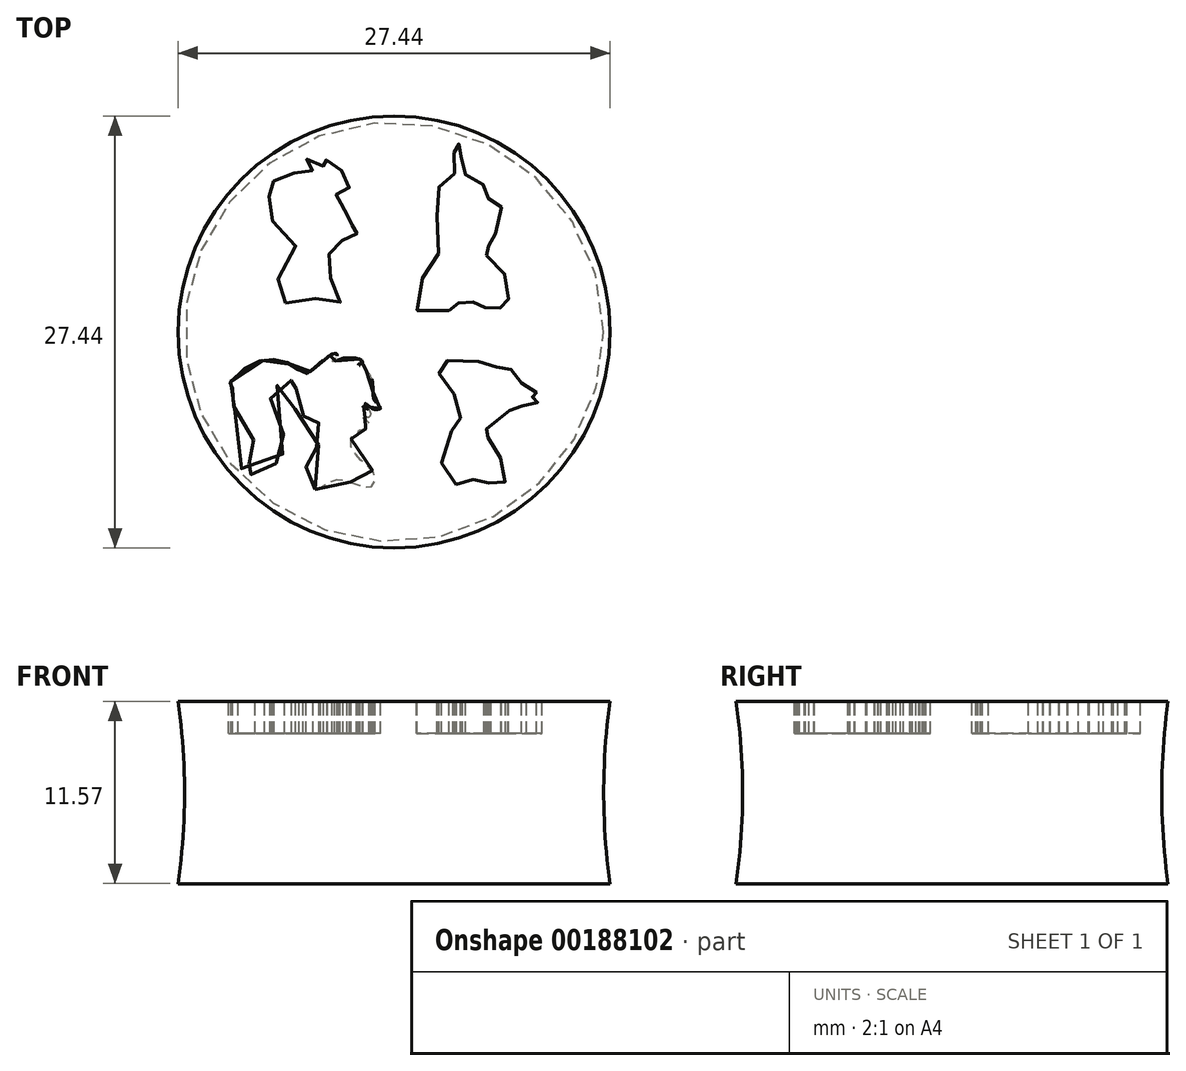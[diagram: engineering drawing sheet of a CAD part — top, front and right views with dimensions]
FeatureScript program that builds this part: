
annotation { "Feature Type Name" : "Feature", "Feature Type Description" : "" }
export const myFeature = defineFeature(function(context is Context, id is Id, definition is map)
    precondition{}
    {
        {
            var Q0;
            Q0=qCreatedBy(makeId("Front.planeOp"),FACE);
            var sketch = newSketch(context, id + "F0", { "sketchPlane" : qUnion([Q0])});
            skLineSegment(sketch, "E0", {"start": v(0, 0) * mm, "end": v(0, -11.57) * mm});
            skLineSegment(sketch, "E1", {"start": v(0, -11.57) * mm, "end": v(13.72, -11.57) * mm});
            skLineSegment(sketch, "E2", {"start": v(13.72, 0) * mm, "end": v(0, 0) * mm});
            skArc(sketch, "E3", {"start": v(13.72, 0) * mm, "mid": v(13.31, -5.79) * mm, "end": v(13.72, -11.57) * mm});
            skSolve(sketch);
        }
        {
            var Q0;
            Q0 = qSketchRegion(id + "F0", true);
            var Q1;
            Q1=sQuery(id+"F0.wireOp",EDGE,"E0");
            revolve(context, id + "F1", {"entities" : qUnion([Q0]), "axis" : qUnion([Q1]), "revolveType" : RevolveType.FULL});
        }
        {
            var Q0;
            Q0=qCreatedBy(makeId("Top.planeOp"),FACE);
            var sketch = newSketch(context, id + "F2", { "sketchPlane" : qUnion([Q0])});
            skFitSpline(sketch, "E4", {"points": [v(-6.9, 1.82) * mm, v(-6.65, 1.93) * mm, v(-6.33, 2.08) * mm, v(-6, 2.27) * mm, v(-5.69, 2.32) * mm, v(-5.44, 2.29) * mm, v(-5.23, 2.26) * mm, v(-4.96, 2.1) * mm, v(-4.72, 1.96) * mm, v(-4.48, 1.85) * mm, v(-4.2, 1.76) * mm, v(-3.95, 1.65) * mm, v(-3.71, 1.64) * mm, v(-3.5, 1.72) * mm, v(-3.43, 1.82) * mm, v(-3.43, 1.96) * mm, v(-3.46, 2.1) * mm, v(-3.5, 2.24) * mm, v(-3.53, 2.4) * mm, v(-3.6, 2.65) * mm, v(-3.67, 2.75) * mm, v(-3.82, 3.04) * mm, v(-3.94, 3.22) * mm, v(-4.01, 3.39) * mm, v(-4.1, 3.55) * mm, v(-4.2, 3.67) * mm, v(-4.2, 3.78) * mm, v(-4.22, 4.06) * mm, v(-4.24, 4.26) * mm, v(-4.24, 4.44) * mm, v(-4.25, 4.6) * mm, v(-4.2, 4.82) * mm, v(-4.1, 4.98) * mm, v(-3.98, 5.2) * mm, v(-3.86, 5.28) * mm, v(-3.73, 5.36) * mm, v(-3.62, 5.44) * mm, v(-3.55, 5.5) * mm, v(-3.5, 5.57) * mm, v(-3.49, 5.63) * mm, v(-3.49, 5.72) * mm, v(-3.49, 5.8) * mm, v(-3.41, 5.8) * mm, v(-3.29, 5.8) * mm, v(-3.17, 5.78) * mm, v(-2.9, 5.78) * mm, v(-2.64, 5.78) * mm, v(-2.5, 5.82) * mm, v(-2.33, 5.88) * mm, v(-2.19, 5.98) * mm, v(-2.16, 6.1) * mm, v(-2.21, 6.18) * mm, v(-2.33, 6.22) * mm, v(-2.5, 6.31) * mm, v(-2.6, 6.4) * mm, v(-2.7, 6.46) * mm, v(-2.8, 6.53) * mm, v(-2.86, 6.61) * mm, v(-2.9, 6.66) * mm, v(-2.97, 6.72) * mm, v(-2.98, 6.73) * mm, v(-2.98, 6.78) * mm, v(-2.92, 6.83) * mm, v(-2.84, 6.8) * mm, v(-2.77, 6.8) * mm, v(-2.64, 6.8) * mm, v(-2.57, 6.82) * mm, v(-2.47, 6.9) * mm, v(-2.4, 7) * mm, v(-2.4, 7.07) * mm, v(-2.43, 7.16) * mm, v(-2.47, 7.22) * mm, v(-2.5, 7.29) * mm, v(-2.54, 7.31) * mm, v(-2.62, 7.31) * mm, v(-2.73, 7.35) * mm, v(-2.82, 7.34) * mm, v(-2.9, 7.32) * mm, v(-2.96, 7.32) * mm, v(-3, 7.32) * mm, v(-3.05, 7.39) * mm, v(-3.14, 7.5) * mm, v(-3.21, 7.57) * mm, v(-3.23, 7.6) * mm, v(-3.26, 7.67) * mm, v(-3.25, 7.74) * mm, v(-3.25, 7.8) * mm, v(-3.25, 7.86) * mm, v(-3.25, 7.9) * mm, v(-3.26, 7.95) * mm, v(-3.27, 7.97) * mm, v(-3.33, 8.1) * mm, v(-3.38, 8.17) * mm, v(-3.41, 8.24) * mm, v(-3.43, 8.29) * mm, v(-3.44, 8.34) * mm, v(-3.44, 8.4) * mm, v(-3.46, 8.46) * mm, v(-3.5, 8.48) * mm, v(-3.55, 8.52) * mm, v(-3.62, 8.57) * mm, v(-3.67, 8.6) * mm, v(-3.73, 8.62) * mm, v(-3.77, 8.65) * mm, v(-3.79, 8.7) * mm, v(-3.79, 8.72) * mm, v(-3.78, 8.73) * mm, v(-3.73, 8.72) * mm, v(-3.67, 8.7) * mm, v(-3.61, 8.69) * mm, v(-3.51, 8.67) * mm, v(-3.43, 8.66) * mm, v(-3.3, 8.66) * mm, v(-3.22, 8.68) * mm, v(-3.18, 8.7) * mm, v(-3.12, 8.72) * mm, v(-3.04, 8.8) * mm, v(-2.96, 8.89) * mm, v(-2.94, 8.95) * mm, v(-2.9, 9.03) * mm, v(-2.87, 9.1) * mm, v(-2.85, 9.17) * mm, v(-2.85, 9.27) * mm, v(-2.85, 9.39) * mm, v(-2.88, 9.54) * mm, v(-2.94, 9.65) * mm, v(-2.98, 9.75) * mm, v(-3.03, 9.83) * mm, v(-3.06, 9.93) * mm, v(-3.11, 10) * mm, v(-3.18, 10.07) * mm, v(-3.2, 10.1) * mm, v(-3.24, 10.15) * mm, v(-3.38, 10.3) * mm, v(-3.47, 10.35) * mm, v(-3.56, 10.46) * mm, v(-3.66, 10.53) * mm, v(-3.71, 10.57) * mm, v(-3.78, 10.62) * mm, v(-3.85, 10.67) * mm, v(-3.9, 10.71) * mm, v(-4.03, 10.8) * mm, v(-4.1, 10.83) * mm, v(-4.18, 10.88) * mm, v(-4.26, 10.9) * mm, v(-4.35, 10.96) * mm, v(-4.43, 11) * mm, v(-4.59, 11.07) * mm, v(-4.65, 11.1) * mm, v(-4.73, 11.08) * mm, v(-4.76, 11) * mm, v(-4.78, 10.88) * mm, v(-4.74, 10.8) * mm, v(-4.64, 10.72) * mm, v(-4.58, 10.64) * mm, v(-4.52, 10.57) * mm, v(-4.48, 10.54) * mm, v(-4.54, 10.56) * mm, v(-4.57, 10.6) * mm, v(-4.63, 10.61) * mm, v(-4.73, 10.65) * mm, v(-4.8, 10.69) * mm, v(-4.86, 10.72) * mm, v(-4.94, 10.76) * mm, v(-5.06, 10.8) * mm, v(-5.09, 10.83) * mm, v(-5.2, 10.88) * mm, v(-5.33, 10.94) * mm, v(-5.43, 10.96) * mm, v(-5.55, 10.97) * mm, v(-5.67, 10.98) * mm, v(-5.74, 10.98) * mm, v(-5.78, 10.91) * mm, v(-5.8, 10.83) * mm, v(-5.77, 10.74) * mm, v(-5.71, 10.67) * mm, v(-5.6, 10.6) * mm, v(-5.47, 10.52) * mm, v(-5.4, 10.44) * mm, v(-5.3, 10.36) * mm, v(-5.22, 10.3) * mm, v(-5.18, 10.24) * mm, v(-5.15, 10.2) * mm, v(-5.14, 10.16) * mm, v(-5.19, 10.14) * mm, v(-5.22, 10.16) * mm, v(-5.3, 10.17) * mm, v(-5.37, 10.2) * mm, v(-5.5, 10.21) * mm, v(-5.74, 10.23) * mm, v(-5.9, 10.22) * mm, v(-6.1, 10.19) * mm, v(-6.33, 10.11) * mm, v(-6.47, 10) * mm, v(-6.64, 9.84) * mm, v(-6.81, 9.64) * mm, v(-6.94, 9.44) * mm, v(-7.05, 9.35) * mm, v(-7.17, 9.35) * mm, v(-7.36, 9.46) * mm, v(-7.54, 9.55) * mm, v(-7.7, 9.6) * mm, v(-7.83, 9.57) * mm, v(-7.85, 9.46) * mm, v(-7.7, 9.08) * mm, v(-7.85, 8.99) * mm, v(-8.02, 8.93) * mm, v(-8.2, 8.83) * mm, v(-8.2, 8.71) * mm, v(-8.04, 8.63) * mm, v(-7.85, 8.57) * mm, v(-7.69, 8.5) * mm, v(-7.65, 8.48) * mm, v(-7.64, 8.4) * mm, v(-7.7, 8.21) * mm, v(-7.76, 7.84) * mm, v(-7.8, 7.6) * mm, v(-7.8, 7.23) * mm, v(-7.72, 7.03) * mm, v(-7.53, 6.76) * mm, v(-7.28, 6.6) * mm, v(-6.81, 6.36) * mm, v(-6.36, 6.01) * mm, v(-6.28, 5.81) * mm, v(-6.25, 5.48) * mm, v(-6.34, 5.13) * mm, v(-6.42, 4.9) * mm, v(-6.46, 4.8) * mm, v(-6.82, 4.13) * mm, v(-7.17, 3.7) * mm, v(-7.33, 3.44) * mm, v(-7.52, 3.04) * mm, v(-7.67, 2.6) * mm, v(-7.7, 2.39) * mm, v(-7.6, 2.16) * mm, v(-7.43, 1.97) * mm, v(-7.23, 1.82) * mm, v(-6.9, 1.82) * mm]});
            skSolve(sketch);
        }
        {
            var Q0;
            Q0 = qSketchRegion(id + "F2", true);
            extrude(context, id + "F3", {"entities" : qUnion([Q0]), "operationType" : NewBodyOperationType.REMOVE, "oppositeDirection" : true, "depth" : 2.03 * mm});
        }
        {
            var Q0;
            Q0=qCreatedBy(makeId("Top.planeOp"),FACE);
            var sketch = newSketch(context, id + "F4", { "sketchPlane" : qUnion([Q0])});
            skFitSpline(sketch, "E5", {"points": [v(3.48, 1.36) * mm, v(3.55, 1.48) * mm, v(3.67, 1.62) * mm, v(3.85, 1.7) * mm, v(4.03, 1.81) * mm, v(4.18, 1.87) * mm, v(4.43, 1.9) * mm, v(4.69, 1.93) * mm, v(4.93, 1.92) * mm, v(5.26, 1.84) * mm, v(5.46, 1.77) * mm, v(5.65, 1.68) * mm, v(5.74, 1.58) * mm, v(5.84, 1.52) * mm, v(6.03, 1.51) * mm, v(6.24, 1.52) * mm, v(6.65, 1.53) * mm, v(7, 1.53) * mm, v(7.22, 1.56) * mm, v(7.26, 1.77) * mm, v(7.25, 2.34) * mm, v(7.24, 3.46) * mm, v(7.23, 3.52) * mm, v(5.9, 4.4) * mm, v(5.88, 4.43) * mm, v(5.87, 4.83) * mm, v(5.87, 4.85) * mm, v(5.77, 4.85) * mm, v(5.75, 4.87) * mm, v(5.72, 5.42) * mm, v(5.71, 5.45) * mm, v(6.15, 5.46) * mm, v(6.14, 5.49) * mm, v(6.13, 6.16) * mm, v(6.13, 6.2) * mm, v(6.78, 6.23) * mm, v(6.8, 6.22) * mm, v(6.81, 7.92) * mm, v(6.82, 7.98) * mm, v(6.02, 8.03) * mm, v(6, 8.03) * mm, v(5.98, 8.57) * mm, v(5.95, 8.68) * mm, v(5.9, 8.83) * mm, v(5.8, 9.07) * mm, v(5.54, 9.52) * mm, v(5.04, 9.8) * mm, v(4.64, 9.94) * mm, v(4.37, 10.13) * mm, v(4.29, 10.5) * mm, v(4.26, 10.97) * mm, v(4.25, 11.4) * mm, v(4.34, 11.5) * mm, v(4.32, 11.8) * mm, v(4.14, 11.94) * mm, v(3.97, 11.94) * mm, v(3.8, 11.85) * mm, v(3.74, 11.65) * mm, v(3.77, 11.42) * mm, v(3.85, 11.36) * mm, v(3.86, 11.29) * mm, v(3.87, 10.15) * mm, v(3.85, 10.08) * mm, v(3.51, 9.87) * mm, v(3.16, 9.58) * mm, v(2.8, 9.11) * mm, v(2.73, 8.42) * mm, v(2.74, 6.98) * mm, v(2.82, 5.4) * mm, v(2.85, 4.33) * mm, v(2.84, 4.3) * mm, v(1.44, 3.17) * mm, v(1.41, 3.15) * mm, v(1.46, 1.32) * mm, v(1.46, 1.3) * mm, v(3.47, 1.31) * mm, v(3.48, 1.36) * mm]});
            skSolve(sketch);
        }
        {
            var Q0;
            Q0 = qSketchRegion(id + "F4", true);
            extrude(context, id + "F5", {"entities" : qUnion([Q0]), "operationType" : NewBodyOperationType.REMOVE, "oppositeDirection" : true, "depth" : 2.03 * mm});
        }
        {
            var Q0;
            Q0=qCreatedBy(makeId("Top.planeOp"),FACE);
            var sketch = newSketch(context, id + "F6", { "sketchPlane" : qUnion([Q0])});
            skFitSpline(sketch, "E6", {"points": [v(-5.02, -10) * mm, v(-4.88, -10) * mm, v(-4.72, -9.94) * mm, v(-4.5, -9.76) * mm, v(-4.18, -9.57) * mm, v(-3.94, -9.42) * mm, v(-3.7, -9.38) * mm, v(-3.5, -9.37) * mm, v(-3.24, -9.4) * mm, v(-3.03, -9.45) * mm, v(-2.75, -9.53) * mm, v(-2.35, -9.68) * mm, v(-2.02, -9.83) * mm, v(-1.73, -9.9) * mm, v(-1.49, -9.86) * mm, v(-1.38, -9.77) * mm, v(-1.33, -9.65) * mm, v(-1.24, -9.47) * mm, v(-1.23, -9.19) * mm, v(-1.28, -8.96) * mm, v(-1.45, -8.71) * mm, v(-1.6, -8.56) * mm, v(-1.8, -8.4) * mm, v(-2.03, -8.21) * mm, v(-2.27, -7.98) * mm, v(-2.42, -7.8) * mm, v(-2.56, -7.58) * mm, v(-2.7, -7.38) * mm, v(-2.72, -7.1) * mm, v(-2.73, -6.8) * mm, v(-2.73, -6.65) * mm, v(-2.72, -6.55) * mm, v(-2.72, -6.5) * mm, v(-2.6, -6.53) * mm, v(-2.52, -6.55) * mm, v(-2.41, -6.55) * mm, v(-2.33, -6.48) * mm, v(-2.28, -6.44) * mm, v(-2.22, -6.36) * mm, v(-2.23, -6.3) * mm, v(-2.23, -6.25) * mm, v(-2.23, -6.2) * mm, v(-2.16, -6.18) * mm, v(-2.11, -6.19) * mm, v(-2.02, -6.2) * mm, v(-1.9, -6.19) * mm, v(-1.79, -6.16) * mm, v(-1.72, -6.1) * mm, v(-1.65, -6.05) * mm, v(-1.6, -6) * mm, v(-1.58, -5.91) * mm, v(-1.59, -5.8) * mm, v(-1.6, -5.73) * mm, v(-1.66, -5.67) * mm, v(-1.69, -5.65) * mm, v(-1.74, -5.63) * mm, v(-1.76, -5.62) * mm, v(-1.83, -5.58) * mm, v(-1.88, -5.55) * mm, v(-1.94, -5.5) * mm, v(-1.98, -5.47) * mm, v(-2, -5.44) * mm, v(-2, -5.41) * mm, v(-1.98, -5.4) * mm, v(-1.98, -5.4) * mm, v(-1.92, -5.41) * mm, v(-1.87, -5.43) * mm, v(-1.8, -5.44) * mm, v(-1.74, -5.43) * mm, v(-1.67, -5.4) * mm, v(-1.57, -5.38) * mm, v(-1.49, -5.27) * mm, v(-1.47, -5.2) * mm, v(-1.48, -5.13) * mm, v(-1.51, -5.06) * mm, v(-1.53, -5) * mm, v(-1.57, -4.97) * mm, v(-1.61, -4.94) * mm, v(-1.72, -4.88) * mm, v(-1.77, -4.85) * mm, v(-1.82, -4.8) * mm, v(-1.9, -4.8) * mm, v(-1.94, -4.77) * mm, v(-1.97, -4.76) * mm, v(-1.98, -4.75) * mm, v(-1.96, -4.72) * mm, v(-1.93, -4.7) * mm, v(-1.9, -4.69) * mm, v(-1.87, -4.66) * mm, v(-1.86, -4.65) * mm, v(-1.84, -4.6) * mm, v(-1.83, -4.56) * mm, v(-1.82, -4.52) * mm, v(-1.76, -4.6) * mm, v(-1.7, -4.63) * mm, v(-1.66, -4.68) * mm, v(-1.59, -4.72) * mm, v(-1.53, -4.78) * mm, v(-1.46, -4.82) * mm, v(-1.29, -4.9) * mm, v(-1.2, -4.92) * mm, v(-1.13, -4.93) * mm, v(-1.07, -4.92) * mm, v(-1, -4.91) * mm, v(-0.94, -4.9) * mm, v(-0.9, -4.88) * mm, v(-0.88, -4.84) * mm, v(-0.88, -4.8) * mm, v(-0.9, -4.74) * mm, v(-0.95, -4.7) * mm, v(-1, -4.65) * mm, v(-1.03, -4.61) * mm, v(-1.08, -4.55) * mm, v(-1.12, -4.5) * mm, v(-1.16, -4.47) * mm, v(-1.2, -4.41) * mm, v(-1.24, -4.35) * mm, v(-1.26, -4.32) * mm, v(-1.3, -4.25) * mm, v(-1.3, -4.18) * mm, v(-1.32, -4.11) * mm, v(-1.32, -4.06) * mm, v(-1.33, -4) * mm, v(-1.33, -3.93) * mm, v(-1.33, -3.88) * mm, v(-1.34, -3.8) * mm, v(-1.33, -3.77) * mm, v(-1.34, -3.7) * mm, v(-1.32, -3.65) * mm, v(-1.34, -3.52) * mm, v(-1.35, -3.45) * mm, v(-1.37, -3.37) * mm, v(-1.37, -3.29) * mm, v(-1.37, -3.2) * mm, v(-1.4, -3.1) * mm, v(-1.4, -3.04) * mm, v(-1.45, -2.92) * mm, v(-1.5, -2.8) * mm, v(-1.55, -2.69) * mm, v(-1.63, -2.59) * mm, v(-1.7, -2.5) * mm, v(-1.79, -2.4) * mm, v(-1.87, -2.35) * mm, v(-1.94, -2.28) * mm, v(-2, -2.23) * mm, v(-2.09, -2.2) * mm, v(-2.15, -2.15) * mm, v(-2.22, -2.11) * mm, v(-2.26, -2.1) * mm, v(-2.28, -2.07) * mm, v(-2.26, -2.05) * mm, v(-2.22, -2.04) * mm, v(-2.17, -2.05) * mm, v(-2.1, -2.04) * mm, v(-2.05, -2.02) * mm, v(-2, -2) * mm, v(-1.99, -1.95) * mm, v(-1.99, -1.91) * mm, v(-2.02, -1.85) * mm, v(-2.06, -1.79) * mm, v(-2.14, -1.75) * mm, v(-2.19, -1.72) * mm, v(-2.25, -1.7) * mm, v(-2.41, -1.68) * mm, v(-2.53, -1.66) * mm, v(-2.67, -1.65) * mm, v(-2.8, -1.66) * mm, v(-2.92, -1.66) * mm, v(-3, -1.66) * mm, v(-3.14, -1.66) * mm, v(-3.22, -1.66) * mm, v(-3.3, -1.69) * mm, v(-3.38, -1.71) * mm, v(-3.47, -1.74) * mm, v(-3.56, -1.78) * mm, v(-3.65, -1.82) * mm, v(-3.75, -1.85) * mm, v(-3.83, -1.86) * mm, v(-3.88, -1.9) * mm, v(-3.93, -1.89) * mm, v(-3.93, -1.87) * mm, v(-3.9, -1.85) * mm, v(-3.87, -1.78) * mm, v(-3.8, -1.74) * mm, v(-3.73, -1.67) * mm, v(-3.65, -1.58) * mm, v(-3.62, -1.52) * mm, v(-3.61, -1.45) * mm, v(-3.63, -1.4) * mm, v(-3.68, -1.37) * mm, v(-3.7, -1.37) * mm, v(-3.81, -1.39) * mm, v(-3.92, -1.4) * mm, v(-4, -1.43) * mm, v(-4.04, -1.45) * mm, v(-4.08, -1.5) * mm, v(-4.2, -1.57) * mm, v(-4.3, -1.63) * mm, v(-4.4, -1.69) * mm, v(-4.52, -1.78) * mm, v(-4.63, -1.84) * mm, v(-4.7, -1.9) * mm, v(-4.78, -1.98) * mm, v(-4.84, -2.05) * mm, v(-4.93, -2.12) * mm, v(-4.99, -2.19) * mm, v(-5.07, -2.27) * mm, v(-5.14, -2.33) * mm, v(-5.23, -2.41) * mm, v(-5.28, -2.5) * mm, v(-5.35, -2.57) * mm, v(-5.4, -2.63) * mm, v(-5.44, -2.66) * mm, v(-5.48, -2.66) * mm, v(-5.54, -2.64) * mm, v(-5.66, -2.6) * mm, v(-5.71, -2.6) * mm, v(-5.8, -2.59) * mm, v(-5.86, -2.6) * mm, v(-5.9, -2.6) * mm, v(-5.97, -2.54) * mm, v(-6.04, -2.44) * mm, v(-6.13, -2.37) * mm, v(-6.2, -2.29) * mm, v(-6.25, -2.23) * mm, v(-6.37, -2.18) * mm, v(-6.5, -2.09) * mm, v(-6.6, -2.03) * mm, v(-6.74, -1.97) * mm, v(-6.9, -1.89) * mm, v(-7.04, -1.86) * mm, v(-7.25, -1.81) * mm, v(-7.42, -1.78) * mm, v(-7.52, -1.76) * mm, v(-7.64, -1.76) * mm, v(-7.89, -1.75) * mm, v(-8.04, -1.75) * mm, v(-8.12, -1.78) * mm, v(-8.33, -1.81) * mm, v(-8.37, -1.82) * mm, v(-8.55, -1.86) * mm, v(-8.66, -1.9) * mm, v(-8.8, -1.94) * mm, v(-8.95, -1.99) * mm, v(-9.23, -2.15) * mm, v(-9.46, -2.28) * mm, v(-9.7, -2.47) * mm, v(-9.87, -2.63) * mm, v(-10.17, -2.92) * mm, v(-10.39, -3.16) * mm, v(-10.49, -3.45) * mm, v(-10.48, -3.73) * mm, v(-10.45, -3.75) * mm, v(-10.4, -3.73) * mm, v(-10.36, -3.67) * mm, v(-10.32, -3.62) * mm, v(-10.28, -3.58) * mm, v(-10.28, -3.63) * mm, v(-10.3, -3.7) * mm, v(-10.35, -3.83) * mm, v(-10.35, -3.98) * mm, v(-10.33, -4.29) * mm, v(-10.1, -4.92) * mm, v(-9.51, -5.87) * mm, v(-8.85, -7.06) * mm, v(-8.86, -7.59) * mm, v(-8.94, -7.96) * mm, v(-9.24, -8.4) * mm, v(-9.9, -8.77) * mm, v(-9.92, -8.8) * mm, v(-9.7, -9.05) * mm, v(-8.8, -8.94) * mm, v(-8.56, -8.75) * mm, v(-8.13, -8.77) * mm, v(-7.32, -8.15) * mm, v(-7.05, -7.7) * mm, v(-6.98, -6.85) * mm, v(-7.24, -5.91) * mm, v(-7.78, -4.57) * mm, v(-7.84, -3.98) * mm, v(-7.5, -3.46) * mm, v(-6.8, -3.11) * mm, v(-6.27, -3.1) * mm, v(-6.26, -3.14) * mm, v(-6.17, -3.34) * mm, v(-6.05, -3.4) * mm, v(-6.05, -3.46) * mm, v(-6.17, -3.53) * mm, v(-6.5, -4.19) * mm, v(-6.32, -4.85) * mm, v(-5.53, -5.41) * mm, v(-5.24, -5.45) * mm, v(-5.2, -5.56) * mm, v(-5.06, -5.68) * mm, v(-4.88, -5.76) * mm, v(-4.77, -5.8) * mm, v(-4.69, -6.36) * mm, v(-4.74, -7.02) * mm, v(-4.91, -7.32) * mm, v(-5.14, -7.5) * mm, v(-5.32, -7.75) * mm, v(-5.56, -8.18) * mm, v(-5.58, -8.78) * mm, v(-5.42, -9.4) * mm, v(-5.21, -9.93) * mm, v(-5.02, -10) * mm]});
            skSolve(sketch);
        }
        {
            var Q0;
            Q0=makeQuery(id+"F6.imprint","IMPRINT",FACE,{"disambiguationData":[TD([[makeQuery(id+"F6.imprint","IMPRINT",EDGE,{"derivedFrom":sQuery(id+"F6.wireOp",EDGE,"E6")}),1.0]])]});
            extrude(context, id + "F7", {"entities" : qUnion([Q0]), "operationType" : NewBodyOperationType.REMOVE, "oppositeDirection" : true, "depth" : 2.03 * mm});
        }
        {
            var Q0;
            Q0=qCreatedBy(makeId("Top.planeOp"),FACE);
            var sketch = newSketch(context, id + "F8", { "sketchPlane" : qUnion([Q0])});
            skFitSpline(sketch, "E7", {"points": [v(3.93, -9.68) * mm, v(4.25, -9.65) * mm, v(4.63, -9.51) * mm, v(4.86, -9.4) * mm, v(5.14, -9.35) * mm, v(5.4, -9.31) * mm, v(5.66, -9.34) * mm, v(5.96, -9.52) * mm, v(6.25, -9.76) * mm, v(6.67, -9.8) * mm, v(6.94, -9.67) * mm, v(7.07, -9.46) * mm, v(7.03, -9.02) * mm, v(6.86, -8.33) * mm, v(6.55, -7.5) * mm, v(6.2, -6.91) * mm, v(5.99, -6.7) * mm, v(5.93, -6.67) * mm, v(5.93, -6.63) * mm, v(5.97, -6.63) * mm, v(6.04, -6.52) * mm, v(6.03, -6.36) * mm, v(5.93, -6.25) * mm, v(5.83, -6.13) * mm, v(5.86, -6.09) * mm, v(5.95, -6.03) * mm, v(6.17, -5.92) * mm, v(6.4, -5.7) * mm, v(6.85, -5.5) * mm, v(7.08, -5.27) * mm, v(7.17, -5.1) * mm, v(7.28, -5) * mm, v(7.5, -4.96) * mm, v(7.7, -4.82) * mm, v(7.8, -4.67) * mm, v(7.88, -4.7) * mm, v(8.15, -4.7) * mm, v(8.36, -4.63) * mm, v(8.47, -4.57) * mm, v(8.8, -4.55) * mm, v(9.14, -4.47) * mm, v(9.4, -4.25) * mm, v(9.3, -4.1) * mm, v(8.87, -4.15) * mm, v(8.78, -4.12) * mm, v(8.64, -4.11) * mm, v(8.42, -4) * mm, v(8.92, -3.97) * mm, v(9.03, -3.87) * mm, v(8.99, -3.73) * mm, v(8.49, -3.31) * mm, v(8.35, -3.29) * mm, v(8.1, -3.26) * mm, v(8.08, -2.96) * mm, v(7.67, -2.31) * mm, v(7.54, -2.32) * mm, v(7.19, -2.5) * mm, v(7.06, -2.48) * mm, v(6.9, -2.29) * mm, v(6.59, -2.3) * mm, v(6.33, -2.1) * mm, v(5.94, -2.09) * mm, v(5.6, -1.9) * mm, v(5.25, -1.9) * mm, v(4.74, -1.72) * mm, v(3.25, -1.85) * mm, v(3.1, -1.93) * mm, v(2.96, -2.08) * mm, v(2.85, -2.4) * mm, v(2.89, -2.74) * mm, v(3.1, -3.27) * mm, v(3.67, -3.84) * mm, v(4.53, -4.76) * mm, v(4.32, -5.45) * mm, v(4.08, -5.46) * mm, v(3.87, -5.82) * mm, v(3.97, -5.99) * mm, v(3.61, -6.34) * mm, v(3.1, -7.35) * mm, v(3.04, -8.6) * mm, v(3.3, -9.44) * mm, v(3.93, -9.68) * mm]});
            skSolve(sketch);
        }
        {
            var Q0;
            Q0 = qSketchRegion(id + "F8", true);
            extrude(context, id + "F9", {"entities" : qUnion([Q0]), "operationType" : NewBodyOperationType.REMOVE, "oppositeDirection" : true, "depth" : 2.03 * mm});
        }
    });
